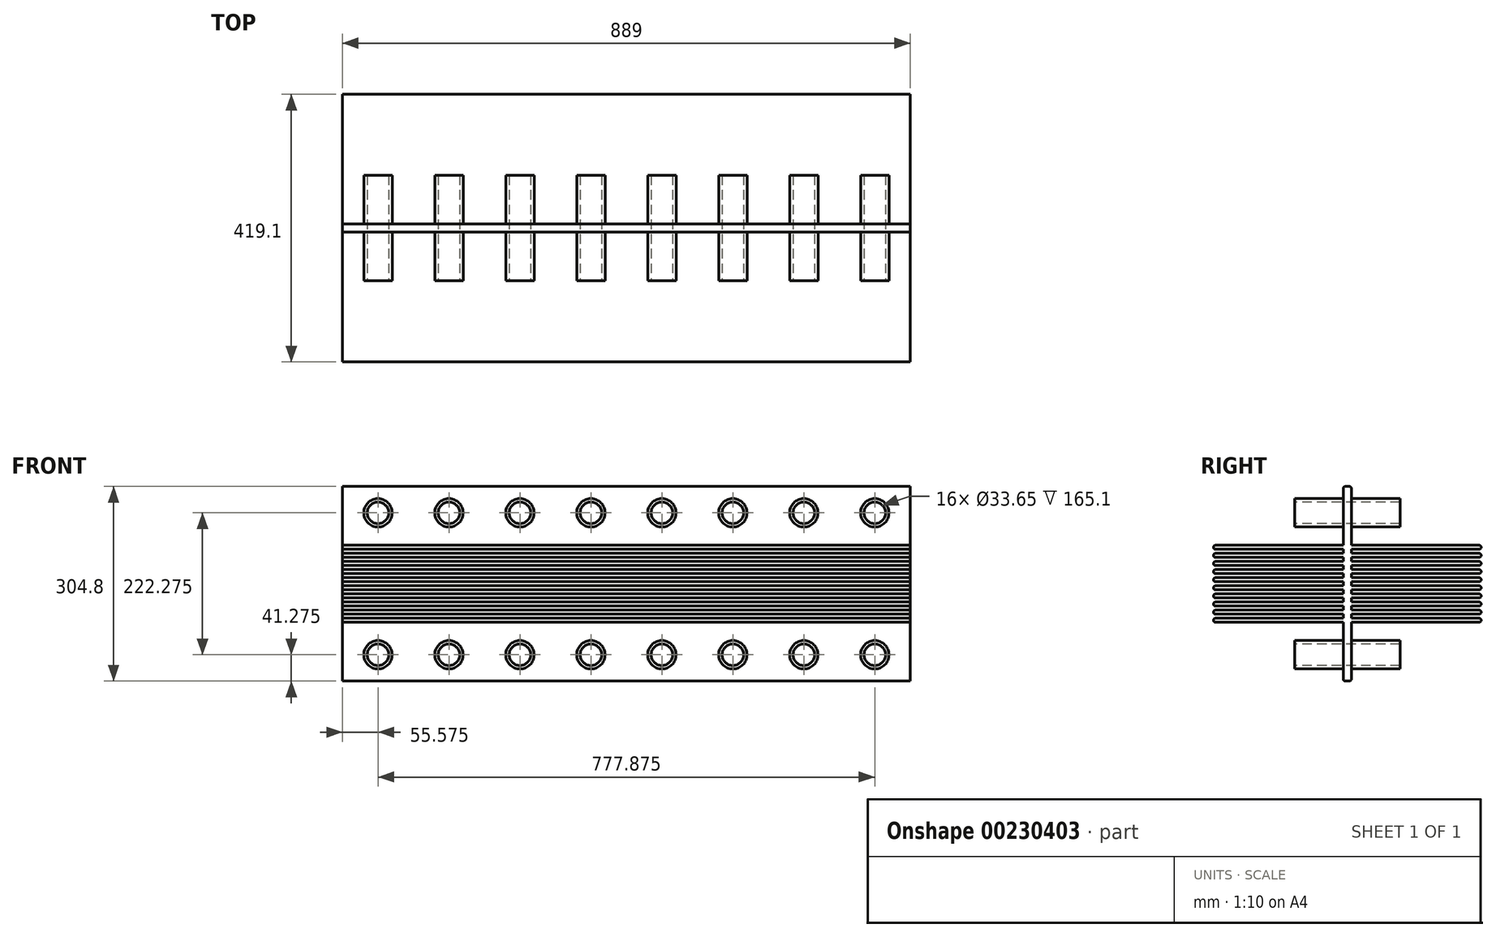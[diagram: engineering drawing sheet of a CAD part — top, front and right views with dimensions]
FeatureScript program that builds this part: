
annotation { "Feature Type Name" : "Feature", "Feature Type Description" : "" }
export const myFeature = defineFeature(function(context is Context, id is Id, definition is map)
    precondition{}
    {
        {
            var Q0;
            Q0=qCreatedBy(makeId("Front.planeOp"),FACE);
            var sketch = newSketch(context, id + "F0", { "sketchPlane" : qUnion([Q0])});
            skLineSegment(sketch, "E0.bottom", {"start": v(0, 0) * mm, "end": v(889, 0) * mm});
            skLineSegment(sketch, "E0.top", {"start": v(0, 304.8) * mm, "end": v(889, 304.8) * mm});
            skLineSegment(sketch, "E0.left", {"start": v(0, 0) * mm, "end": v(0, 304.8) * mm});
            skLineSegment(sketch, "E0.right", {"start": v(889, 0) * mm, "end": v(889, 304.8) * mm});
            skSolve(sketch);
        }
        {
            var Q0;
            Q0 = qSketchRegion(id + "F0", true);
            extrude(context, id + "F1", {"entities" : qUnion([Q0]), "depth" : 12.7 * mm});
        }
        {
            var Q0;
            Q0=makeQuery(id+"F1.opExtrude","CAP_FACE",FACE,{"disambiguationData":[OSD([sQuery(id+"F0.wireOp",EDGE,"E0.bottom"),sQuery(id+"F0.wireOp",EDGE,"E0.top"),sQuery(id+"F0.wireOp",EDGE,"E0.left"),sQuery(id+"F0.wireOp",EDGE,"E0.right")])],"isStart":false});
            var sketch = newSketch(context, id + "F2", { "sketchPlane" : qUnion([Q0])});
            skPoint(sketch, "E1", {"position": v(55.58, 41.28) * mm});
            skPoint(sketch, "E2.0.1.0", {"position": v(55.58, 263.55) * mm});
            skPoint(sketch, "E2.1.0.0", {"position": v(166.7, 41.28) * mm});
            skPoint(sketch, "E2.1.1.0", {"position": v(166.7, 263.55) * mm});
            skPoint(sketch, "E2.2.0.0", {"position": v(277.83, 41.28) * mm});
            skPoint(sketch, "E2.2.1.0", {"position": v(277.83, 263.55) * mm});
            skPoint(sketch, "E2.3.0.0", {"position": v(388.95, 41.28) * mm});
            skPoint(sketch, "E2.3.1.0", {"position": v(388.95, 263.55) * mm});
            skPoint(sketch, "E2.4.0.0", {"position": v(500.08, 41.28) * mm});
            skPoint(sketch, "E2.4.1.0", {"position": v(500.08, 263.55) * mm});
            skPoint(sketch, "E2.5.0.0", {"position": v(611.2, 41.28) * mm});
            skPoint(sketch, "E2.5.1.0", {"position": v(611.2, 263.55) * mm});
            skPoint(sketch, "E2.6.0.0", {"position": v(722.33, 41.28) * mm});
            skPoint(sketch, "E2.6.1.0", {"position": v(722.33, 263.55) * mm});
            skPoint(sketch, "E2.7.0.0", {"position": v(833.45, 41.28) * mm});
            skPoint(sketch, "E2.7.1.0", {"position": v(833.45, 263.55) * mm});
            skLineSegment(sketch, "E2.direction1", {"start": v(55.58, 41.28) * mm, "end": v(166.7, 41.28) * mm, "construction": true});
            skLineSegment(sketch, "E2.direction2", {"start": v(55.58, 41.28) * mm, "end": v(55.58, 263.55) * mm, "construction": true});
            skSolve(sketch);
        }
        {
            var Q0;
            Q0=sQuery(id+"F2.wireOp",VERTEX,"E1");
            var Q1;
            Q1=sQuery(id+"F2.wireOp",VERTEX,"E2.0.1.0");
            var Q2;
            Q2=sQuery(id+"F2.wireOp",VERTEX,"E2.1.1.0");
            var Q3;
            Q3=sQuery(id+"F2.wireOp",VERTEX,"E2.1.0.0");
            var Q4;
            Q4=sQuery(id+"F2.wireOp",VERTEX,"E2.2.0.0");
            var Q5;
            Q5=sQuery(id+"F2.wireOp",VERTEX,"E2.2.1.0");
            var Q6;
            Q6=sQuery(id+"F2.wireOp",VERTEX,"E2.3.1.0");
            var Q7;
            Q7=sQuery(id+"F2.wireOp",VERTEX,"E2.4.0.0");
            var Q8;
            Q8=sQuery(id+"F2.wireOp",VERTEX,"E2.4.1.0");
            var Q9;
            Q9=sQuery(id+"F2.wireOp",VERTEX,"E2.3.0.0");
            var Q10;
            Q10=sQuery(id+"F2.wireOp",VERTEX,"E2.5.0.0");
            var Q11;
            Q11=sQuery(id+"F2.wireOp",VERTEX,"E2.6.0.0");
            var Q12;
            Q12=sQuery(id+"F2.wireOp",VERTEX,"E2.7.0.0");
            var Q13;
            Q13=sQuery(id+"F2.wireOp",VERTEX,"E2.7.1.0");
            var Q14;
            Q14=sQuery(id+"F2.wireOp",VERTEX,"E2.6.1.0");
            var Q15;
            Q15=sQuery(id+"F2.wireOp",VERTEX,"E2.5.1.0");
            var Q16;
            Q16=makeQuery(id+"F1.opExtrude","SWEPT_BODY",BODY,{"disambiguationData":[OSD([sQuery(id+"F0.wireOp",EDGE,"E0.bottom"),sQuery(id+"F0.wireOp",EDGE,"E0.top"),sQuery(id+"F0.wireOp",EDGE,"E0.left"),sQuery(id+"F0.wireOp",EDGE,"E0.right")])]});
            hole(context, id + "F3", {"style" : HoleStyle.SIMPLE, "endStyle" : HoleEndStyle.THROUGH, "holeDiameter" : 33.65 * mm, "locations" : qUnion([Q0, Q1, Q2, Q3, Q4, Q5, Q6, Q7, Q8, Q9, Q10, Q11, Q12, Q13, Q14, Q15]), "scope" : qUnion([Q16]), "isTappedThrough" : true});
        }
        {
            var Q0;
            Q0=makeQuery(id+"F1.opExtrude","SWEPT_FACE",FACE,{"disambiguationData":[OSD([sQuery(id+"F0.wireOp",EDGE,"E0.left")])]});
            var sketch = newSketch(context, id + "F4", { "sketchPlane" : qUnion([Q0])});
            skLineSegment(sketch, "E3", {"start": v(12.7, 152.4) * mm, "end": v(159.55, 152.4) * mm, "construction": true});
            skPoint(sketch, "E3.endSnap0", {"position": v(12.7, 152.4) * mm});
            skLineSegment(sketch, "E4.bottom", {"start": v(12.7, 161.93) * mm, "end": v(212.72, 161.93) * mm});
            skLineSegment(sketch, "E4.top", {"start": v(12.7, 155.58) * mm, "end": v(212.72, 155.58) * mm});
            skLineSegment(sketch, "E4.left", {"start": v(12.7, 161.93) * mm, "end": v(12.7, 155.58) * mm});
            skLineSegment(sketch, "E4.right", {"start": v(215.9, 158.75) * mm, "end": v(215.9, 158.75) * mm});
            skPoint(sketch, "E5.visualSharp", {"position": v(215.9, 161.93) * mm});
            skArc(sketch, "E5.filletArc", {"start": v(215.9, 158.75) * mm, "mid": v(214.97, 161) * mm, "end": v(212.72, 161.93) * mm});
            skPoint(sketch, "E6.visualSharp", {"position": v(215.9, 155.58) * mm});
            skArc(sketch, "E6.filletArc", {"start": v(212.72, 155.58) * mm, "mid": v(214.97, 156.5) * mm, "end": v(215.9, 158.75) * mm});
            skLineSegment(sketch, "E7.bottom", {"start": v(12.7, 174.63) * mm, "end": v(212.72, 174.63) * mm});
            skLineSegment(sketch, "E7.top", {"start": v(12.7, 168.28) * mm, "end": v(212.72, 168.28) * mm});
            skLineSegment(sketch, "E7.left", {"start": v(12.7, 174.63) * mm, "end": v(12.7, 168.28) * mm});
            skLineSegment(sketch, "E7.right", {"start": v(215.9, 171.45) * mm, "end": v(215.9, 171.45) * mm});
            skPoint(sketch, "E8.visualSharp", {"position": v(215.9, 174.63) * mm});
            skArc(sketch, "E8.filletArc", {"start": v(215.9, 171.45) * mm, "mid": v(214.97, 173.7) * mm, "end": v(212.72, 174.63) * mm});
            skPoint(sketch, "E9.visualSharp", {"position": v(215.9, 168.28) * mm});
            skArc(sketch, "E9.filletArc", {"start": v(212.72, 168.28) * mm, "mid": v(214.97, 169.2) * mm, "end": v(215.9, 171.45) * mm});
            skLineSegment(sketch, "E10.bottom", {"start": v(12.7, 187.33) * mm, "end": v(212.72, 187.33) * mm});
            skLineSegment(sketch, "E10.top", {"start": v(12.7, 180.98) * mm, "end": v(212.72, 180.98) * mm});
            skLineSegment(sketch, "E10.left", {"start": v(12.7, 187.33) * mm, "end": v(12.7, 180.98) * mm});
            skLineSegment(sketch, "E10.right", {"start": v(215.9, 184.15) * mm, "end": v(215.9, 184.15) * mm});
            skPoint(sketch, "E11.visualSharp", {"position": v(215.9, 187.33) * mm});
            skArc(sketch, "E11.filletArc", {"start": v(215.9, 184.15) * mm, "mid": v(214.97, 186.4) * mm, "end": v(212.72, 187.33) * mm});
            skPoint(sketch, "E12.visualSharp", {"position": v(215.9, 180.98) * mm});
            skArc(sketch, "E12.filletArc", {"start": v(212.72, 180.98) * mm, "mid": v(214.97, 181.9) * mm, "end": v(215.9, 184.15) * mm});
            skLineSegment(sketch, "E13.bottom", {"start": v(12.7, 200.03) * mm, "end": v(212.72, 200.03) * mm});
            skLineSegment(sketch, "E13.top", {"start": v(12.7, 193.68) * mm, "end": v(212.72, 193.68) * mm});
            skLineSegment(sketch, "E13.left", {"start": v(12.7, 200.03) * mm, "end": v(12.7, 193.68) * mm});
            skLineSegment(sketch, "E13.right", {"start": v(215.9, 196.85) * mm, "end": v(215.9, 196.85) * mm});
            skPoint(sketch, "E14.visualSharp", {"position": v(215.9, 200.03) * mm});
            skArc(sketch, "E14.filletArc", {"start": v(215.9, 196.85) * mm, "mid": v(214.97, 199.1) * mm, "end": v(212.72, 200.03) * mm});
            skPoint(sketch, "E15.visualSharp", {"position": v(215.9, 193.68) * mm});
            skArc(sketch, "E15.filletArc", {"start": v(212.72, 193.68) * mm, "mid": v(214.97, 194.6) * mm, "end": v(215.9, 196.85) * mm});
            skLineSegment(sketch, "E16.bottom", {"start": v(12.7, 212.73) * mm, "end": v(212.72, 212.73) * mm});
            skLineSegment(sketch, "E16.top", {"start": v(12.7, 206.38) * mm, "end": v(212.72, 206.38) * mm});
            skLineSegment(sketch, "E16.left", {"start": v(12.7, 212.73) * mm, "end": v(12.7, 206.38) * mm});
            skLineSegment(sketch, "E16.right", {"start": v(215.9, 209.55) * mm, "end": v(215.9, 209.55) * mm});
            skPoint(sketch, "E17.visualSharp", {"position": v(215.9, 212.73) * mm});
            skArc(sketch, "E17.filletArc", {"start": v(215.9, 209.55) * mm, "mid": v(214.97, 211.8) * mm, "end": v(212.72, 212.73) * mm});
            skPoint(sketch, "E18.visualSharp", {"position": v(215.9, 206.38) * mm});
            skArc(sketch, "E18.filletArc", {"start": v(212.72, 206.38) * mm, "mid": v(214.97, 207.3) * mm, "end": v(215.9, 209.55) * mm});
            skLineSegment(sketch, "E19.MirrorCS", {"start": v(12.7, 92.07) * mm, "end": v(12.7, 98.42) * mm});
            skLineSegment(sketch, "E20.MirrorCS", {"start": v(12.7, 104.77) * mm, "end": v(12.7, 111.12) * mm});
            skLineSegment(sketch, "E21.MirrorCS", {"start": v(12.7, 117.47) * mm, "end": v(12.7, 123.82) * mm});
            skLineSegment(sketch, "E22.MirrorCS", {"start": v(12.7, 130.17) * mm, "end": v(12.7, 136.53) * mm});
            skLineSegment(sketch, "E23.MirrorCS", {"start": v(12.7, 142.88) * mm, "end": v(12.7, 149.22) * mm});
            skLineSegment(sketch, "E24.MirrorCS", {"start": v(12.7, 142.88) * mm, "end": v(212.72, 142.88) * mm});
            skLineSegment(sketch, "E25.MirrorCS", {"start": v(12.7, 149.22) * mm, "end": v(212.72, 149.22) * mm});
            skLineSegment(sketch, "E26.MirrorCS", {"start": v(12.7, 130.17) * mm, "end": v(212.72, 130.17) * mm});
            skLineSegment(sketch, "E27.MirrorCS", {"start": v(12.7, 136.53) * mm, "end": v(212.72, 136.53) * mm});
            skLineSegment(sketch, "E28.MirrorCS", {"start": v(12.7, 123.82) * mm, "end": v(212.72, 123.82) * mm});
            skLineSegment(sketch, "E29.MirrorCS", {"start": v(12.7, 117.47) * mm, "end": v(212.72, 117.47) * mm});
            skLineSegment(sketch, "E30.MirrorCS", {"start": v(12.7, 111.12) * mm, "end": v(212.72, 111.12) * mm});
            skLineSegment(sketch, "E31.MirrorCS", {"start": v(12.7, 104.77) * mm, "end": v(212.72, 104.77) * mm});
            skLineSegment(sketch, "E32.MirrorCS", {"start": v(12.7, 98.42) * mm, "end": v(212.72, 98.42) * mm});
            skLineSegment(sketch, "E33.MirrorCS", {"start": v(12.7, 92.07) * mm, "end": v(212.72, 92.07) * mm});
            skArc(sketch, "E34.MirrorCS", {"start": v(215.9, 95.25) * mm, "mid": v(214.97, 93) * mm, "end": v(212.72, 92.07) * mm});
            skArc(sketch, "E35.MirrorCS", {"start": v(212.72, 98.42) * mm, "mid": v(214.97, 97.5) * mm, "end": v(215.9, 95.25) * mm});
            skArc(sketch, "E36.MirrorCS", {"start": v(215.9, 107.95) * mm, "mid": v(214.97, 105.7) * mm, "end": v(212.72, 104.77) * mm});
            skArc(sketch, "E37.MirrorCS", {"start": v(212.72, 111.12) * mm, "mid": v(214.97, 110.2) * mm, "end": v(215.9, 107.95) * mm});
            skArc(sketch, "E38.MirrorCS", {"start": v(215.9, 120.65) * mm, "mid": v(214.97, 118.4) * mm, "end": v(212.72, 117.47) * mm});
            skArc(sketch, "E39.MirrorCS", {"start": v(212.72, 123.82) * mm, "mid": v(214.97, 122.9) * mm, "end": v(215.9, 120.65) * mm});
            skArc(sketch, "E40.MirrorCS", {"start": v(215.9, 133.35) * mm, "mid": v(214.97, 131.1) * mm, "end": v(212.72, 130.17) * mm});
            skArc(sketch, "E41.MirrorCS", {"start": v(212.72, 136.53) * mm, "mid": v(214.97, 135.6) * mm, "end": v(215.9, 133.35) * mm});
            skArc(sketch, "E42.MirrorCS", {"start": v(215.9, 146.05) * mm, "mid": v(214.97, 143.8) * mm, "end": v(212.72, 142.88) * mm});
            skArc(sketch, "E43.MirrorCS", {"start": v(212.72, 149.22) * mm, "mid": v(214.97, 148.3) * mm, "end": v(215.9, 146.05) * mm});
            skLineSegment(sketch, "E44", {"start": v(6.35, 304.8) * mm, "end": v(6.35, 0) * mm, "construction": true});
            skLineSegment(sketch, "E45.MirrorCS", {"start": v(0, 212.73) * mm, "end": v(0, 206.38) * mm});
            skLineSegment(sketch, "E46.MirrorCS", {"start": v(0, 200.03) * mm, "end": v(0, 193.68) * mm});
            skLineSegment(sketch, "E47.MirrorCS", {"start": v(0, 187.33) * mm, "end": v(0, 180.98) * mm});
            skLineSegment(sketch, "E48.MirrorCS", {"start": v(0, 174.63) * mm, "end": v(0, 168.28) * mm});
            skLineSegment(sketch, "E49.MirrorCS", {"start": v(0, 161.93) * mm, "end": v(0, 155.58) * mm});
            skLineSegment(sketch, "E50.MirrorCS", {"start": v(0, 142.88) * mm, "end": v(0, 149.22) * mm});
            skLineSegment(sketch, "E51.MirrorCS", {"start": v(0, 130.17) * mm, "end": v(0, 136.53) * mm});
            skLineSegment(sketch, "E52.MirrorCS", {"start": v(0, 117.47) * mm, "end": v(0, 123.82) * mm});
            skLineSegment(sketch, "E53.MirrorCS", {"start": v(0, 104.77) * mm, "end": v(0, 111.12) * mm});
            skLineSegment(sketch, "E54.MirrorCS", {"start": v(0, 92.07) * mm, "end": v(0, 98.42) * mm});
            skLineSegment(sketch, "E55.MirrorCS", {"start": v(0, 98.42) * mm, "end": v(-200.02, 98.42) * mm});
            skLineSegment(sketch, "E56.MirrorCS", {"start": v(0, 92.07) * mm, "end": v(-200.02, 92.07) * mm});
            skLineSegment(sketch, "E57.MirrorCS", {"start": v(0, 104.77) * mm, "end": v(-200.02, 104.77) * mm});
            skLineSegment(sketch, "E58.MirrorCS", {"start": v(0, 111.12) * mm, "end": v(-200.02, 111.12) * mm});
            skLineSegment(sketch, "E59.MirrorCS", {"start": v(0, 117.47) * mm, "end": v(-200.02, 117.47) * mm});
            skLineSegment(sketch, "E60.MirrorCS", {"start": v(0, 123.82) * mm, "end": v(-200.02, 123.82) * mm});
            skLineSegment(sketch, "E61.MirrorCS", {"start": v(0, 130.17) * mm, "end": v(-200.02, 130.17) * mm});
            skLineSegment(sketch, "E62.MirrorCS", {"start": v(0, 136.53) * mm, "end": v(-200.02, 136.53) * mm});
            skLineSegment(sketch, "E63.MirrorCS", {"start": v(0, 142.88) * mm, "end": v(-200.02, 142.88) * mm});
            skLineSegment(sketch, "E64.MirrorCS", {"start": v(0, 149.22) * mm, "end": v(-200.02, 149.22) * mm});
            skLineSegment(sketch, "E65.MirrorCS", {"start": v(0, 155.58) * mm, "end": v(-200.02, 155.58) * mm});
            skLineSegment(sketch, "E66.MirrorCS", {"start": v(0, 161.93) * mm, "end": v(-200.02, 161.93) * mm});
            skLineSegment(sketch, "E67.MirrorCS", {"start": v(0, 168.28) * mm, "end": v(-200.02, 168.28) * mm});
            skLineSegment(sketch, "E68.MirrorCS", {"start": v(0, 174.63) * mm, "end": v(-200.02, 174.63) * mm});
            skLineSegment(sketch, "E69.MirrorCS", {"start": v(0, 180.98) * mm, "end": v(-200.02, 180.98) * mm});
            skLineSegment(sketch, "E70.MirrorCS", {"start": v(0, 187.33) * mm, "end": v(-200.02, 187.33) * mm});
            skLineSegment(sketch, "E71.MirrorCS", {"start": v(0, 193.68) * mm, "end": v(-200.02, 193.68) * mm});
            skLineSegment(sketch, "E72.MirrorCS", {"start": v(0, 200.03) * mm, "end": v(-200.02, 200.03) * mm});
            skLineSegment(sketch, "E73.MirrorCS", {"start": v(0, 206.38) * mm, "end": v(-200.02, 206.38) * mm});
            skLineSegment(sketch, "E74.MirrorCS", {"start": v(0, 212.73) * mm, "end": v(-200.02, 212.73) * mm});
            skArc(sketch, "E75.MirrorCS", {"start": v(-203.2, 209.55) * mm, "mid": v(-202.27, 211.8) * mm, "end": v(-200.02, 212.73) * mm});
            skArc(sketch, "E76.MirrorCS", {"start": v(-200.02, 206.38) * mm, "mid": v(-202.27, 207.3) * mm, "end": v(-203.2, 209.55) * mm});
            skArc(sketch, "E77.MirrorCS", {"start": v(-203.2, 196.85) * mm, "mid": v(-202.27, 199.1) * mm, "end": v(-200.02, 200.03) * mm});
            skArc(sketch, "E78.MirrorCS", {"start": v(-200.02, 193.68) * mm, "mid": v(-202.27, 194.6) * mm, "end": v(-203.2, 196.85) * mm});
            skArc(sketch, "E79.MirrorCS", {"start": v(-203.2, 184.15) * mm, "mid": v(-202.27, 186.4) * mm, "end": v(-200.02, 187.33) * mm});
            skArc(sketch, "E80.MirrorCS", {"start": v(-200.02, 180.98) * mm, "mid": v(-202.27, 181.9) * mm, "end": v(-203.2, 184.15) * mm});
            skArc(sketch, "E81.MirrorCS", {"start": v(-203.2, 171.45) * mm, "mid": v(-202.27, 173.7) * mm, "end": v(-200.02, 174.63) * mm});
            skArc(sketch, "E82.MirrorCS", {"start": v(-200.02, 168.28) * mm, "mid": v(-202.27, 169.2) * mm, "end": v(-203.2, 171.45) * mm});
            skArc(sketch, "E83.MirrorCS", {"start": v(-203.2, 158.75) * mm, "mid": v(-202.27, 161) * mm, "end": v(-200.02, 161.93) * mm});
            skArc(sketch, "E84.MirrorCS", {"start": v(-200.02, 155.58) * mm, "mid": v(-202.27, 156.5) * mm, "end": v(-203.2, 158.75) * mm});
            skArc(sketch, "E85.MirrorCS", {"start": v(-200.02, 149.22) * mm, "mid": v(-202.27, 148.3) * mm, "end": v(-203.2, 146.05) * mm});
            skArc(sketch, "E86.MirrorCS", {"start": v(-203.2, 146.05) * mm, "mid": v(-202.27, 143.8) * mm, "end": v(-200.02, 142.88) * mm});
            skArc(sketch, "E87.MirrorCS", {"start": v(-200.02, 136.53) * mm, "mid": v(-202.27, 135.6) * mm, "end": v(-203.2, 133.35) * mm});
            skArc(sketch, "E88.MirrorCS", {"start": v(-203.2, 133.35) * mm, "mid": v(-202.27, 131.1) * mm, "end": v(-200.02, 130.17) * mm});
            skArc(sketch, "E89.MirrorCS", {"start": v(-200.02, 123.82) * mm, "mid": v(-202.27, 122.9) * mm, "end": v(-203.2, 120.65) * mm});
            skArc(sketch, "E90.MirrorCS", {"start": v(-203.2, 120.65) * mm, "mid": v(-202.27, 118.4) * mm, "end": v(-200.02, 117.47) * mm});
            skArc(sketch, "E91.MirrorCS", {"start": v(-200.02, 111.12) * mm, "mid": v(-202.27, 110.2) * mm, "end": v(-203.2, 107.95) * mm});
            skArc(sketch, "E92.MirrorCS", {"start": v(-203.2, 107.95) * mm, "mid": v(-202.27, 105.7) * mm, "end": v(-200.02, 104.77) * mm});
            skArc(sketch, "E93.MirrorCS", {"start": v(-200.02, 98.42) * mm, "mid": v(-202.27, 97.5) * mm, "end": v(-203.2, 95.25) * mm});
            skArc(sketch, "E94.MirrorCS", {"start": v(-203.2, 95.25) * mm, "mid": v(-202.27, 93) * mm, "end": v(-200.02, 92.07) * mm});
            skSolve(sketch);
        }
        {
            var Q0;
            Q0 = qSketchRegion(id + "F4", true);
            var Q1;
            Q1=makeQuery(id+"F1.opExtrude","SWEPT_FACE",FACE,{"disambiguationData":[OSD([sQuery(id+"F0.wireOp",EDGE,"E0.right")])]});
            extrude(context, id + "F5", {"entities" : qUnion([Q0]), "operationType" : NewBodyOperationType.ADD, "endBound" : BoundingType.UP_TO_SURFACE, "oppositeDirection" : true, "endBoundEntityFace" : qUnion([Q1]), "depth" : 25.4 * mm});
        }
        {
            var Q0;
            Q0=makeQuery(id+"F1.opExtrude","CAP_EDGE",EDGE,{"disambiguationData":[OSD([sQuery(id+"F0.wireOp",EDGE,"E0.bottom")])],"isStart":true});
            var Q1;
            Q1=makeQuery(id+"F1.opExtrude","CAP_EDGE",EDGE,{"disambiguationData":[OSD([sQuery(id+"F0.wireOp",EDGE,"E0.bottom")])],"isStart":false});
            var Q2;
            Q2=makeQuery(id+"F1.opExtrude","CAP_EDGE",EDGE,{"disambiguationData":[OSD([sQuery(id+"F0.wireOp",EDGE,"E0.top")])],"isStart":false});
            var Q3;
            Q3=makeQuery(id+"F1.opExtrude","CAP_EDGE",EDGE,{"disambiguationData":[OSD([sQuery(id+"F0.wireOp",EDGE,"E0.top")])],"isStart":true});
            fillet(context, id + "F6", {"entities" : qUnion([Q0, Q1, Q2, Q3]), "radius" : 3.17 * mm, "tangentPropagation" : true, "allowEdgeOverflow" : false});
        }
        {
            var Q0;
            {var subQ5=sQuery(id+"F0.wireOp",EDGE,"E0.right");var subQ81=sQuery(id+"F0.wireOp",EDGE,"E0.bottom");var subQ87=sQuery(id+"F0.wireOp",EDGE,"E0.left");Q0=makeQuery(id+"F5.boolean.opBoolean","SPLIT",FACE,{"disambiguationData":[TD([makeQuery(id+"F1.opExtrude","SWEPT_FACE",FACE,{"disambiguationData":[OSD([subQ81])]})])],"derivedFrom":makeQuery(id+"F1.opExtrude","CAP_FACE",FACE,{"disambiguationData":[OSD([subQ81,sQuery(id+"F0.wireOp",EDGE,"E0.top"),subQ87,subQ5])],"isStart":true})});}
            var sketch = newSketch(context, id + "F7", { "sketchPlane" : qUnion([Q0])});
            skCircle(sketch, "E95.0", {"center": v(-55.58, 41.28) * mm, "radius": 16.83 * mm});
            skCircle(sketch, "E96", {"center": v(-55.58, 41.28) * mm, "radius": 22.24 * mm});
            skCircle(sketch, "E97.0.1.0", {"center": v(-55.58, 263.55) * mm, "radius": 22.24 * mm});
            skCircle(sketch, "E97.0.1.1", {"center": v(-55.58, 263.55) * mm, "radius": 16.83 * mm});
            skCircle(sketch, "E97.1.0.0", {"center": v(-166.7, 41.28) * mm, "radius": 22.24 * mm});
            skCircle(sketch, "E97.1.0.1", {"center": v(-166.7, 41.28) * mm, "radius": 16.83 * mm});
            skCircle(sketch, "E97.1.1.0", {"center": v(-166.7, 263.55) * mm, "radius": 22.24 * mm});
            skCircle(sketch, "E97.1.1.1", {"center": v(-166.7, 263.55) * mm, "radius": 16.83 * mm});
            skCircle(sketch, "E97.2.0.0", {"center": v(-277.83, 41.28) * mm, "radius": 22.24 * mm});
            skCircle(sketch, "E97.2.0.1", {"center": v(-277.83, 41.28) * mm, "radius": 16.83 * mm});
            skCircle(sketch, "E97.2.1.0", {"center": v(-277.83, 263.55) * mm, "radius": 22.24 * mm});
            skCircle(sketch, "E97.2.1.1", {"center": v(-277.83, 263.55) * mm, "radius": 16.83 * mm});
            skCircle(sketch, "E97.3.0.0", {"center": v(-388.95, 41.28) * mm, "radius": 22.24 * mm});
            skCircle(sketch, "E97.3.0.1", {"center": v(-388.95, 41.28) * mm, "radius": 16.83 * mm});
            skCircle(sketch, "E97.3.1.0", {"center": v(-388.95, 263.55) * mm, "radius": 22.24 * mm});
            skCircle(sketch, "E97.3.1.1", {"center": v(-388.95, 263.55) * mm, "radius": 16.83 * mm});
            skCircle(sketch, "E97.4.0.0", {"center": v(-500.08, 41.28) * mm, "radius": 22.24 * mm});
            skCircle(sketch, "E97.4.0.1", {"center": v(-500.08, 41.28) * mm, "radius": 16.83 * mm});
            skCircle(sketch, "E97.4.1.0", {"center": v(-500.08, 263.55) * mm, "radius": 22.24 * mm});
            skCircle(sketch, "E97.4.1.1", {"center": v(-500.08, 263.55) * mm, "radius": 16.83 * mm});
            skCircle(sketch, "E97.5.0.0", {"center": v(-611.2, 41.28) * mm, "radius": 22.24 * mm});
            skCircle(sketch, "E97.5.0.1", {"center": v(-611.2, 41.28) * mm, "radius": 16.83 * mm});
            skCircle(sketch, "E97.5.1.0", {"center": v(-611.2, 263.55) * mm, "radius": 22.24 * mm});
            skCircle(sketch, "E97.5.1.1", {"center": v(-611.2, 263.55) * mm, "radius": 16.83 * mm});
            skCircle(sketch, "E97.6.0.0", {"center": v(-722.33, 41.28) * mm, "radius": 22.24 * mm});
            skCircle(sketch, "E97.6.0.1", {"center": v(-722.33, 41.28) * mm, "radius": 16.83 * mm});
            skCircle(sketch, "E97.6.1.0", {"center": v(-722.33, 263.55) * mm, "radius": 22.24 * mm});
            skCircle(sketch, "E97.6.1.1", {"center": v(-722.33, 263.55) * mm, "radius": 16.83 * mm});
            skCircle(sketch, "E97.7.0.0", {"center": v(-833.45, 41.28) * mm, "radius": 22.24 * mm});
            skCircle(sketch, "E97.7.0.1", {"center": v(-833.45, 41.28) * mm, "radius": 16.83 * mm});
            skCircle(sketch, "E97.7.1.0", {"center": v(-833.45, 263.55) * mm, "radius": 22.24 * mm});
            skCircle(sketch, "E97.7.1.1", {"center": v(-833.45, 263.55) * mm, "radius": 16.83 * mm});
            skLineSegment(sketch, "E97.direction1", {"start": v(-55.58, 41.28) * mm, "end": v(-166.7, 41.28) * mm, "construction": true});
            skLineSegment(sketch, "E97.direction2", {"start": v(-55.58, 41.28) * mm, "end": v(-55.58, 263.55) * mm, "construction": true});
            skSolve(sketch);
        }
        {
            var Q0;
            Q0 = qSketchRegion(id + "F7", true);
            extrude(context, id + "F8", {"entities" : qUnion([Q0]), "operationType" : NewBodyOperationType.ADD, "depth" : 76.2 * mm});
        }
        {
            var Q0;
            Q0=makeQuery(id+"F2.imprint","IMPRINT",FACE,{"disambiguationData":[TD([[makeQuery(id+"F2.imprint","IMPRINT",EDGE,{"derivedFrom":makeQuery(id+"F1.opExtrude","CAP_EDGE",EDGE,{"disambiguationData":[OSD([sQuery(id+"F0.wireOp",EDGE,"E0.bottom")])],"isStart":false})}),1.0]])]});
            var sketch = newSketch(context, id + "F9", { "sketchPlane" : qUnion([Q0])});
            skCircle(sketch, "E98.0", {"center": v(55.58, 41.28) * mm, "radius": 16.83 * mm});
            skCircle(sketch, "E99", {"center": v(55.58, 41.28) * mm, "radius": 22.24 * mm});
            skCircle(sketch, "E100.0.1.0", {"center": v(55.58, 263.55) * mm, "radius": 22.24 * mm});
            skCircle(sketch, "E100.0.1.1", {"center": v(55.58, 263.55) * mm, "radius": 16.83 * mm});
            skCircle(sketch, "E100.1.0.0", {"center": v(166.7, 41.28) * mm, "radius": 22.24 * mm});
            skCircle(sketch, "E100.1.0.1", {"center": v(166.7, 41.28) * mm, "radius": 16.83 * mm});
            skCircle(sketch, "E100.1.1.0", {"center": v(166.7, 263.55) * mm, "radius": 22.24 * mm});
            skCircle(sketch, "E100.1.1.1", {"center": v(166.7, 263.55) * mm, "radius": 16.83 * mm});
            skCircle(sketch, "E100.2.0.0", {"center": v(277.83, 41.28) * mm, "radius": 22.24 * mm});
            skCircle(sketch, "E100.2.0.1", {"center": v(277.83, 41.28) * mm, "radius": 16.83 * mm});
            skCircle(sketch, "E100.2.1.0", {"center": v(277.83, 263.55) * mm, "radius": 22.24 * mm});
            skCircle(sketch, "E100.2.1.1", {"center": v(277.83, 263.55) * mm, "radius": 16.83 * mm});
            skCircle(sketch, "E100.3.0.0", {"center": v(388.95, 41.28) * mm, "radius": 22.24 * mm});
            skCircle(sketch, "E100.3.0.1", {"center": v(388.95, 41.28) * mm, "radius": 16.83 * mm});
            skCircle(sketch, "E100.3.1.0", {"center": v(388.95, 263.55) * mm, "radius": 22.24 * mm});
            skCircle(sketch, "E100.3.1.1", {"center": v(388.95, 263.55) * mm, "radius": 16.83 * mm});
            skCircle(sketch, "E100.4.0.0", {"center": v(500.08, 41.28) * mm, "radius": 22.24 * mm});
            skCircle(sketch, "E100.4.0.1", {"center": v(500.08, 41.28) * mm, "radius": 16.83 * mm});
            skCircle(sketch, "E100.4.1.0", {"center": v(500.08, 263.55) * mm, "radius": 22.24 * mm});
            skCircle(sketch, "E100.4.1.1", {"center": v(500.08, 263.55) * mm, "radius": 16.83 * mm});
            skCircle(sketch, "E100.5.0.0", {"center": v(611.2, 41.28) * mm, "radius": 22.24 * mm});
            skCircle(sketch, "E100.5.0.1", {"center": v(611.2, 41.28) * mm, "radius": 16.83 * mm});
            skCircle(sketch, "E100.5.1.0", {"center": v(611.2, 263.55) * mm, "radius": 22.24 * mm});
            skCircle(sketch, "E100.5.1.1", {"center": v(611.2, 263.55) * mm, "radius": 16.83 * mm});
            skCircle(sketch, "E100.6.0.0", {"center": v(722.33, 41.28) * mm, "radius": 22.24 * mm});
            skCircle(sketch, "E100.6.0.1", {"center": v(722.33, 41.28) * mm, "radius": 16.83 * mm});
            skCircle(sketch, "E100.6.1.0", {"center": v(722.33, 263.55) * mm, "radius": 22.24 * mm});
            skCircle(sketch, "E100.6.1.1", {"center": v(722.33, 263.55) * mm, "radius": 16.83 * mm});
            skCircle(sketch, "E100.7.0.0", {"center": v(833.45, 41.28) * mm, "radius": 22.24 * mm});
            skCircle(sketch, "E100.7.0.1", {"center": v(833.45, 41.28) * mm, "radius": 16.83 * mm});
            skCircle(sketch, "E100.7.1.0", {"center": v(833.45, 263.55) * mm, "radius": 22.24 * mm});
            skCircle(sketch, "E100.7.1.1", {"center": v(833.45, 263.55) * mm, "radius": 16.83 * mm});
            skLineSegment(sketch, "E100.direction1", {"start": v(55.58, 41.28) * mm, "end": v(166.7, 41.28) * mm, "construction": true});
            skLineSegment(sketch, "E100.direction2", {"start": v(55.58, 41.28) * mm, "end": v(55.58, 263.55) * mm, "construction": true});
            skSolve(sketch);
        }
        {
            var Q0;
            Q0 = qSketchRegion(id + "F9", true);
            extrude(context, id + "F10", {"entities" : qUnion([Q0]), "operationType" : NewBodyOperationType.ADD, "depth" : 76.2 * mm});
        }
    });
